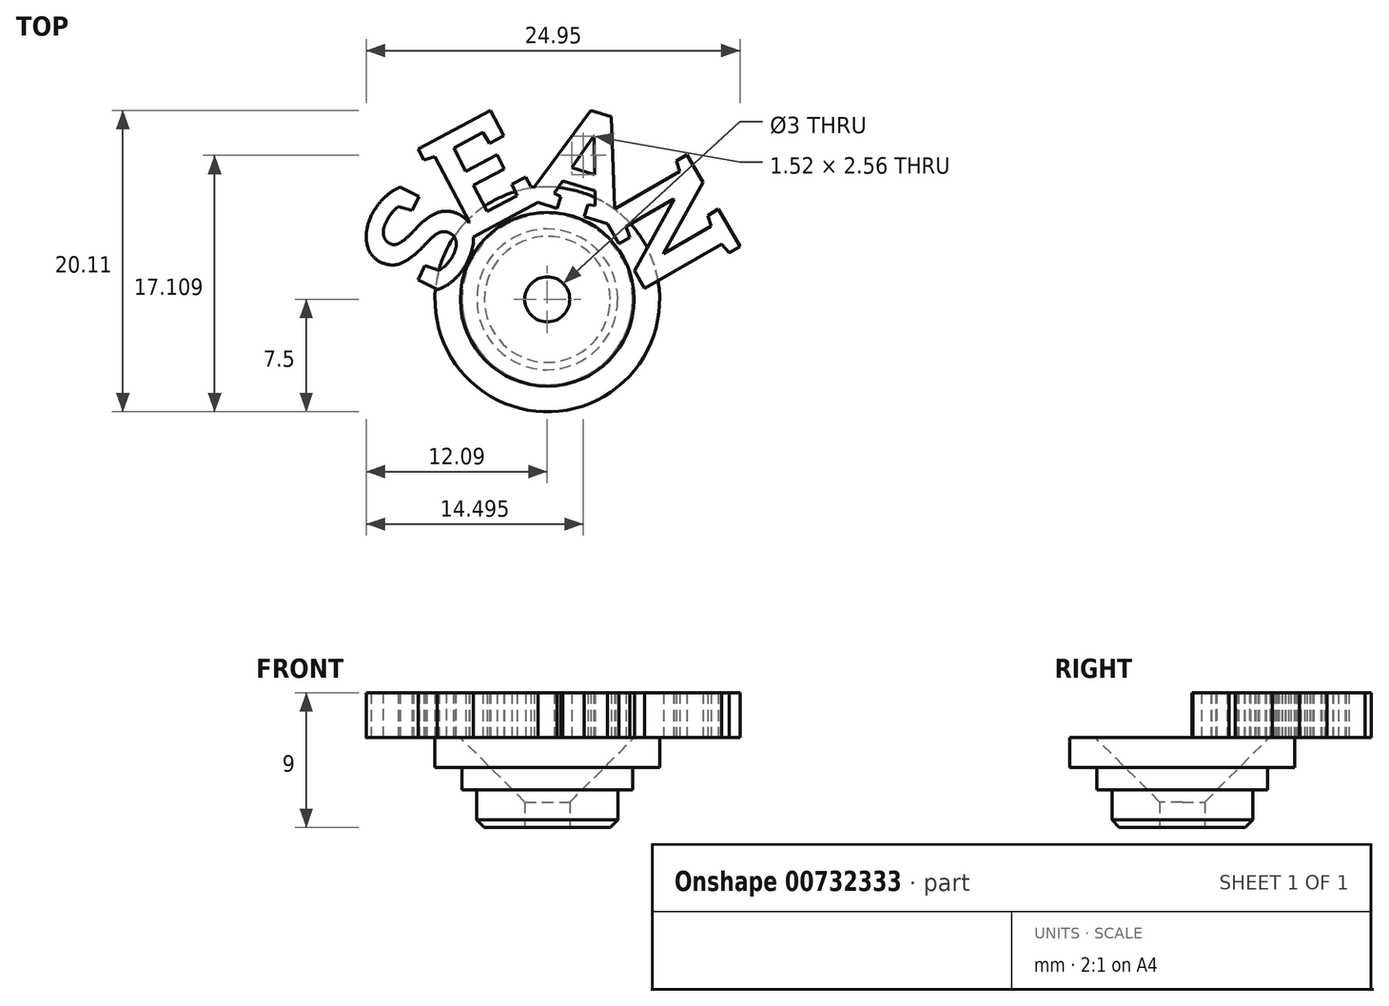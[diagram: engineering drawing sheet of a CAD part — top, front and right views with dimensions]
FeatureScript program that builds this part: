
annotation { "Feature Type Name" : "Feature", "Feature Type Description" : "" }
export const myFeature = defineFeature(function(context is Context, id is Id, definition is map)
    precondition{}
    {
        {
            var Q0;
            Q0=qCreatedBy(makeId("Top.planeOp"),FACE);
            var sketch = newSketch(context, id + "F0", { "sketchPlane" : qUnion([Q0])});
            skCircle(sketch, "E0", {"center": v(0, 0) * mm, "radius": 7.5 * mm});
            skLineSegment(sketch, "E1", {"start": v(0, 19.33) * mm, "end": v(0, -22.56) * mm, "construction": true});
            skLineSegment(sketch, "E2", {"start": v(17.52, 0) * mm, "end": v(-21.05, 0) * mm, "construction": true});
            skSolve(sketch);
        }
        {
            var Q0;
            Q0=qSketchRegion(id+"F0",true);
            extrude(context, id + "F1", {"entities" : qUnion([Q0]), "depth" : 2 * mm, "offsetDistance" : 25 * mm});
        }
        {
            var Q0;
            Q0=makeQuery(id+"F1.opExtrude","CAP_FACE",FACE,{"disambiguationData":[OSD([sQuery(id+"F0.wireOp",EDGE,"E0")])],"isStart":true});
            var sketch = newSketch(context, id + "F2", { "sketchPlane" : qUnion([Q0])});
            skCircle(sketch, "E3", {"center": v(0, 0) * mm, "radius": 4.7 * mm});
            skSolve(sketch);
        }
        {
            var Q0;
            Q0=qSketchRegion(id+"F2",true);
            extrude(context, id + "F3", {"entities" : qUnion([Q0]), "operationType" : NewBodyOperationType.ADD, "depth" : 4 * mm, "offsetDistance" : 25 * mm});
        }
        {
            var Q0;
            Q0=makeQuery(id+"F3.opExtrude","CAP_EDGE",EDGE,{"disambiguationData":[OSD([sQuery(id+"F2.wireOp",EDGE,"E3")])],"isStart":false});
            chamfer(context, id + "F4", {"entities" : qUnion([Q0]), "width" : .5 * mm, "tangentPropagation" : true});
        }
        {
            var Q0;
            Q0=makeQuery(id+"F3.opExtrude","CAP_FACE",FACE,{"disambiguationData":[OSD([sQuery(id+"F2.wireOp",EDGE,"E3")])],"isStart":false});
            var sketch = newSketch(context, id + "F5", { "sketchPlane" : qUnion([Q0])});
            skCircle(sketch, "E4", {"center": v(0, 0) * mm, "radius": 1.5 * mm});
            skSolve(sketch);
        }
        {
            var Q0;
            Q0=qSketchRegion(id+"F5",true);
            extrude(context, id + "F6", {"entities" : qUnion([Q0]), "operationType" : NewBodyOperationType.REMOVE, "oppositeDirection" : true, "depth" : 25 * mm, "offsetDistance" : 25 * mm});
        }
        {
            var Q0;
            Q0=makeQuery(id+"F1.opExtrude","CAP_FACE",FACE,{"disambiguationData":[OSD([sQuery(id+"F0.wireOp",EDGE,"E0")])],"isStart":true});
            var sketch = newSketch(context, id + "F7", { "sketchPlane" : qUnion([Q0])});
            skCircle(sketch, "E5.0", {"center": v(0, 0) * mm, "radius": 5.7 * mm});
            skCircle(sketch, "E6.0", {"center": v(0, 0) * mm, "radius": 4.7 * mm});
            skSolve(sketch);
        }
        {
            var Q0;
            Q0=qSketchRegion(id+"F7",true);
            extrude(context, id + "F8", {"entities" : qUnion([Q0]), "operationType" : NewBodyOperationType.ADD, "depth" : 1.5 * mm, "offsetDistance" : 25 * mm});
        }
        {
            var Q0;
            Q0=makeQuery(id+"F1.opExtrude","CAP_FACE",FACE,{"disambiguationData":[OSD([sQuery(id+"F0.wireOp",EDGE,"E0")])],"isStart":false});
            var sketch = newSketch(context, id + "F9", { "sketchPlane" : qUnion([Q0])});
            skText(sketch, "E7", { "text": "S", "fontName": "RobotoSlab-Bold.ttf"});
            skText(sketch, "E8", { "text": "E", "fontName": "RobotoSlab-Bold.ttf"});
            skText(sketch, "E9", { "text": "N", "fontName": "RobotoSlab-Bold.ttf"});
            skText(sketch, "E10", { "text": "A", "fontName": "RobotoSlab-Bold.ttf"});
            skLineSegment(sketch, "E11", {"start": v(0, 0) * mm, "end": v(-13.7, 6.68) * mm, "construction": true});
            skLineSegment(sketch, "E12", {"start": v(0, 0) * mm, "end": v(13.74, 7.93) * mm, "construction": true});
            skLineSegment(sketch, "E13", {"start": v(0, 0) * mm, "end": v(4.98, 16.3) * mm, "construction": true});
            skLineSegment(sketch, "E14", {"start": v(0, 0) * mm, "end": v(-7.52, 14.14) * mm, "construction": true});
            skLineSegment(sketch, "E15", {"start": v(0, 0) * mm, "end": v(21.4, 0) * mm, "construction": true});
            const initialGuessF9  = {"E7": [-0.00675, -0.00016, 0.43837, 0.8988, 0.007], "E8": [-0.00561, 0.00381, 0.88295, 0.46947, 0.007], "E9": [0.00321, 0.00643, 0.5, -0.86603, 0.007], "E10": [-0.00178, 0.00682, 0.9563, -0.29237, 0.007]};
            skSetInitialGuess(sketch, initialGuessF9);
            skSolve(sketch);
        }
        {
            var Q0;
            Q0 = qSketchRegion(id + "F9", true);
            extrude(context, id + "F10", {"entities" : qUnion([Q0]), "operationType" : NewBodyOperationType.ADD, "depth" : 3 * mm, "offsetDistance" : 25 * mm});
        }
        {
            var Q0;
            Q0=makeQuery(id+"F6.boolean.opBoolean","INTERSECT",EDGE,{"derivedFrom":[makeQuery(id+"F1.opExtrude","CAP_FACE",FACE,{"disambiguationData":[OSD([sQuery(id+"F0.wireOp",EDGE,"E0")])],"isStart":false}),makeQuery(id+"F6.opExtrude","SWEPT_FACE",FACE,{"disambiguationData":[OSD([sQuery(id+"F5.wireOp",EDGE,"E4")])]})]});
            chamfer(context, id + "F11", {"entities" : qUnion([Q0]), "width" : 4.3 * mm, "tangentPropagation" : true});
        }
    });
